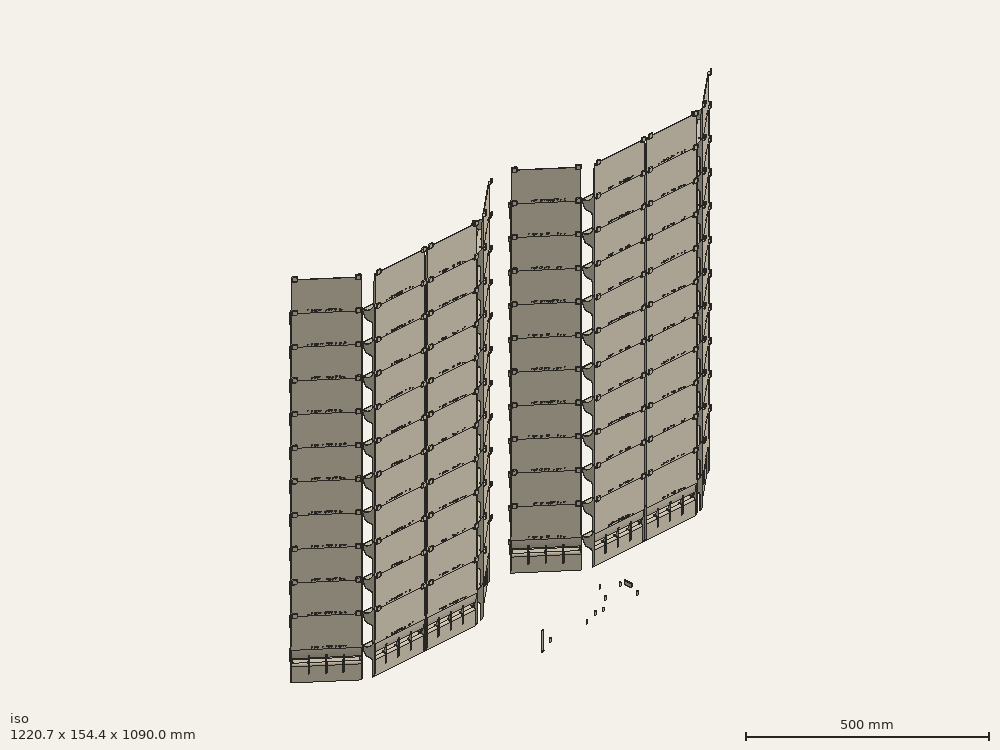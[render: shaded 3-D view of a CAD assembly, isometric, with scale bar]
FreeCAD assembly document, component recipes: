
FREECAD ASSEMBLY — COMPONENT RECIPES ("composit_stand8")

This assembly document has 28 components, labeled P0..P27 below (a component is one placed body or linked part). 26 of them carry a construction recipe — the FreeCAD feature program that regenerates the part from scratch, quoted from this document or its linked companion documents; the rest are supplied as boundary geometry only. No exploded tour is included for this assembly.
NOTE — document 2 of 2 of this assembly tour. The two overview renders and the header above are repeated from document 1; the component sections below continue where the previous document stopped.
COMPONENT P24 — recipe-attached ("module_Body", modeled in this document).
Construction recipe (the document's own serialized feature program — sketch geometry with constraints, then the solid features built on it; lengths are millimeters unless a unit is written):

FEATURE [PartDesign::SubShapeBinder] Binder
  BindCopyOnChange = 0
  BindMode = 0
  ClaimChildren = true
  Context = -> Body [Binder.]
  Fuse = false
  MakeFace = true
  OffsetFill = false
  OffsetIntersection = false
  OffsetJoinType = 0
  OffsetOpenResult = false
  PartialLoad = false
  Relative = false
  Support = -> [Connect]
  _Version = 2
FEATURE [PartDesign::FeaturePython] BaseBend  # WARN: FeaturePython — macro-defined, semantics opaque (R4)
  BendSide = 1
  BendSketch = -> Binder
  MidPlane = false
  Reverse = false
  Suppressed = false
  length = 1100
  radius = 0.1
  thickness = 0.3
  expr: length = <<Properties>>.modules_fix_height
FEATURE [PartDesign::CoordinateSystem] Local_CS005  label="face_base_LCS"
  AttacherType = Attacher::AttachEngine3D
  AttachmentSupport = -> [XY_Plane]
  MapMode = 5
FEATURE [PartDesign::FeaturePython] Extend  # WARN: FeaturePython — macro-defined, semantics opaque (R4)
  BaseFeature = -> BaseBend
  Offset = 0.02
  Refine = true
  Suppressed = false
  UseSubtraction = false
  baseObject = -> BaseBend [Face1]
  gap1 = 0
  gap2 = 0
  length = 0
FEATURE [PartDesign::FeaturePython] Bend  # WARN: FeaturePython — macro-defined, semantics opaque (R4)
  AutoMiter = false
  BaseFeature = -> Extend
  BendType = 0
  LengthList = [0.1]
  LengthSpec = 0
  ReliefFactor = 0.7
  Suppressed = false
  UseReliefFactor = false
  angle = 90
  baseObject = -> Extend [Edge119,Edge104,Edge124,Edge75,Edge58,Edge122,Edge29,Edge14]
  bendAList = [90]
  extend1 = 0
  extend2 = 0
  gap1 = 0
  gap2 = 0
  invert = true
  kfactor = 0.5
  length = 0.1
  maxExtendDist = 5
  minGap = 0.2
  minReliefGap = 1
  miterangle1 = 0
  miterangle2 = 0
  offset = 0
  radius = 0.1
  reliefType = 0
  reliefd = 1
  reliefw = 0.8
  sketchflip = false
  sketchinvert = false
  unfold = false
  expr: radius = BaseBend.radius
FEATURE [PartDesign::CoordinateSystem] Local_CS009  label="face_section_LCS"
  AttacherType = Attacher::AttachEngine3D
  AttachmentOffset = pos=(319.563,20,0) rot=(0,0,1;0rad)
  AttachmentSupport = -> [XY_Plane]
  MapMode = 5
  Placement = pos=(319.563,20,0) rot=(0,0,1;0rad)
  expr: .AttachmentOffset.Base.x = <<mid_Sketch>>.Constraints.middle
  expr: .AttachmentOffset.Base.y = <<base_Sketch>>.Constraints.offset
FEATURE [PartDesign::CoordinateSystem] Local_CS006  label="sink1_LCS"
  AttacherType = Attacher::AttachEngine3D
  AttachmentOffset = pos=(0,0,100) rot=(0,0,1;0rad)
  AttachmentSupport = -> [Local_CS009]
  MapMode = 5
  Placement = pos=(319.563,20,100) rot=(0,0,1;0rad)
  expr: .AttachmentOffset.Base.z = <<sink_placement>>.Placement.Base.z
FEATURE [PartDesign::CoordinateSystem] Local_CS007  label="sink2_LCS"
  AttacherType = Attacher::AttachEngine3D
  AttachmentOffset = pos=(-639.126,0,0) rot=(0,0,1;0rad)
  AttachmentSupport = -> [Local_CS006]
  MapMode = 5
  Placement = pos=(-319.563,20,100) rot=(0,0,1;0rad)
  expr: .AttachmentOffset.Base.x = -<<mid_Sketch>>.Constraints.middle * 2
FEATURE [PartDesign::CoordinateSystem] Local_CS010  label="dropper_comp_fix1_LCS"
  AttacherType = Attacher::AttachEngine3D
  AttachmentOffset = pos=(0,0,1100) rot=(0,0,1;0rad)
  AttachmentSupport = -> [Local_CS009]
  MapMode = 5
  Placement = pos=(319.563,20,1100) rot=(0,0,1;0rad)
  expr: .AttachmentOffset.Base.z = <<Properties>>.modules_fix_height
FEATURE [PartDesign::CoordinateSystem] Local_CS011  label="dropper_comp_fix2_LCS"
  AttacherType = Attacher::AttachEngine3D
  AttachmentOffset = pos=(-639.126,0,0) rot=(0,0,1;0rad)
  AttachmentSupport = -> [Local_CS010]
  MapMode = 5
  Placement = pos=(-319.563,20,1100) rot=(0,0,1;0rad)
  expr: .AttachmentOffset.Base.x = -<<mid_Sketch>>.Constraints.middle * 2
FEATURE [PartDesign::CoordinateSystem] Local_CS014  label="bar1_LCS"
  AttacherType = Attacher::AttachEngine3D
  AttachmentSupport = -> [LinearArray004]
  MapMode = 1
  Placement = pos=(-636.126,17,220) rot=(0.707107,0,0.707107;3.14159rad)
FEATURE [PartDesign::CoordinateSystem] Local_CS015  label="bar2_LCS"
  AttacherType = Attacher::AttachEngine3D
  AttachmentSupport = -> [LinearArray004]
  MapMode = 1
  Placement = pos=(-636.126,17,883.5) rot=(0.707107,0,0.707107;3.14159rad)
FEATURE [PartDesign::CoordinateSystem] Local_CS024
  AttacherType = Attacher::AttachEngine3D
  AttachmentOffset = pos=(319.563,0,0) rot=(0,1,0;3.14159rad)
  AttachmentSupport = -> [XY_Plane]
  MapMode = 5
  Placement = pos=(319.563,0,0) rot=(0,1,0;3.14159rad)
  expr: .AttachmentOffset.Base.x = <<mid_Sketch>>.Constraints.middle
FEATURE [PartDesign::CoordinateSystem] Local_CS025  label="face_lamp_fix_LCS"
  AttacherType = Attacher::AttachEngine3D
  AttachmentOffset = pos=(319.563,0,182) rot=(0,0,1;0rad)
  AttachmentSupport = -> [XY_Plane]
  MapMode = 5
  Placement = pos=(319.563,0,182) rot=(0,0,1;0rad)
  expr: AttachmentOffset = <<face_lamp_fix_placement>>.Placement
FEATURE [PartDesign::CoordinateSystem] Local_CS029
  AttacherType = Attacher::AttachEngine3D
  AttachmentOffset = pos=(164.635,0,0) rot=(0,0,1;0rad)
  AttachmentSupport = -> [Local_CS006]
  MapMode = 5
  Placement = pos=(484.198,20,100) rot=(0,0,1;0rad)
  expr: .AttachmentOffset.Base.x = <<base_Sketch>>.Constraints.face / 2
FEATURE [Sketcher::SketchObject] Sketch075
  AttachmentOffset = pos=(0,0,0) rot=(0,0.707107,0.707107;3.14159rad)
  AttachmentSupport = -> [Local_CS029]
  FullyConstrained = true
  MapMode = 5
  Placement = pos=(484.198,20,100) rot=(0,0.707107,0.707107;3.14159rad)
  expr: Constraints[19] = <<Dimensions>>.Constraints.modules_face / 2
  sketch-geometry (7):
    g0: LineSegment StartX=164.635 StartY=0 StartZ=0 EndX=-1 EndY=0 EndZ=0
    g1: LineSegment StartX=-1 StartY=0 StartZ=0 EndX=-1 EndY=15 EndZ=0
    g2: LineSegment StartX=-1 StartY=15 StartZ=0 EndX=1 EndY=15 EndZ=0
    g3: ArcOfCircle CenterX=1 CenterY=0 CenterZ=0 NormalX=0 NormalY=0 NormalZ=1 AngleXU=0 Radius=15 StartAngle=0.339837 EndAngle=1.5708
    g4: ArcOfCircle CenterX=17.9706 CenterY=6 CenterZ=0 NormalX=0 NormalY=0 NormalZ=1 AngleXU=0 Radius=3 StartAngle=3.48143 EndAngle=4.71239
    g5: LineSegment StartX=164.635 StartY=0 StartZ=0 EndX=164.635 EndY=3 EndZ=0
    g6: LineSegment StartX=164.635 StartY=3 StartZ=0 EndX=17.9706 EndY=3 EndZ=0
  constraints (20):
    c: PointOnObject(g0,g-1)
    c: Horizontal(g0)
    c: Coincident(g0,g1)
    c: Vertical(g1)
    c: Coincident(g1,g2)
    c: Horizontal(g2)
    c: PointOnObject(g3,g-1)
    c: Tangent(g3,g2) = 1.5708
    c: Tangent(g4,g3) = 1.5708
    c: Radius(g4) = 3
    c: Radius(g3) = 15
    c: DistanceX(g2) = 1
    c: DistanceX(g1) = -1
    c: Coincident(g0,g5)
    c: Vertical(g5)
    c: Coincident(g5,g6)
    c: Horizontal(g6)
    c: Tangent(g6,g4) = 1.5708
    c: DistanceY(g5) = 3
    c: DistanceX(g0) = 164.635
FEATURE [Sketcher::SketchObject] Sketch076
  AttachmentOffset = pos=(0,0,0) rot=(0.889126,0.323616,0.323616;1.68804rad)
  AttachmentSupport = -> [Local_CS029]
  FullyConstrained = true
  MapMode = 5
  Placement = pos=(484.198,20,100) rot=(0.889126,0.323616,0.323616;1.68804rad)
  expr: .AttachmentOffset.Rotation.Yaw = <<base_Sketch>>.Constraints.angle
  sketch-geometry (5):
    g0: LineSegment StartX=18.7482 StartY=0 StartZ=0 EndX=-1 EndY=0 EndZ=0
    g1: LineSegment StartX=-1 StartY=0 StartZ=0 EndX=-1 EndY=15 EndZ=0
    g2: LineSegment StartX=-1 StartY=15 StartZ=0 EndX=1 EndY=15 EndZ=0
    g3: ArcOfCircle CenterX=1 CenterY=0 CenterZ=0 NormalX=0 NormalY=0 NormalZ=1 AngleXU=0 Radius=15 StartAngle=0.167448 EndAngle=1.5708
    g4: ArcOfCircle CenterX=18.7482 CenterY=3 CenterZ=0 NormalX=0 NormalY=0 NormalZ=1 AngleXU=0 Radius=3 StartAngle=3.30904 EndAngle=4.71239
  constraints (14):
    c: PointOnObject(g0,g-1)
    c: PointOnObject(g0,g-1)
    c: Coincident(g0,g1)
    c: Vertical(g1)
    c: Coincident(g1,g2)
    c: Horizontal(g2)
    c: PointOnObject(g3,g-1)
    c: Tangent(g3,g2) = 1.5708
    c: Tangent(g4,g0) = 1.5708
    c: Tangent(g4,g3) = 1.5708
    c: DistanceX(g2) = 1
    c: DistanceY(g1,g1) = 15
    c: DistanceX(g1) = -1
    c: Radius(g4) = 3
FEATURE [PartDesign::Plane] DatumPlane004
  AttachmentSupport = -> [Local_CS006]
  Length = 65.8114
  MapMode = 4
  Placement = pos=(319.563,20,100) rot=(0.57735,0.57735,0.57735;2.0944rad)
  ResizeMode = 0
  Width = 140.811
FEATURE [PartDesign::Plane] DatumPlane005
  AttachmentSupport = -> [Local_CS005]
  Length = 60
  MapMode = 4
  Placement = pos=(0,0,0) rot=(0.57735,0.57735,0.57735;2.0944rad)
  ResizeMode = 0
  Width = 60
FEATURE [PartDesign::Mirrored] Mirrored008
  MirrorPlane = -> DatumPlane004
  Suppressed = false
FEATURE [PartDesign::LinearPattern] LinearPattern004
  Direction = -> Sketch075 [H_Axis]
  Length = 639.126
  Mode = 0
  Occurrences = 2
  Offset = 639.126
  Suppressed = false
  expr: Length = <<Dimensions>>.Constraints.modules_middle_distance * 2
FEATURE [PartDesign::CoordinateSystem] Local_CS032  label="face_top_LCS"
  AttacherType = Attacher::AttachEngine3D
  AttachmentOffset = pos=(0,0,1100) rot=(0,0,1;0rad)
  AttachmentSupport = -> [XY_Plane]
  MapMode = 5
  Placement = pos=(0,0,1100) rot=(0,0,1;0rad)
  expr: .AttachmentOffset.Base.z = <<Properties>>.modules_fix_height
FEATURE [PartDesign::CoordinateSystem] Local_CS034
  AttacherType = Attacher::AttachEngine3D
  AttachmentOffset = pos=(-639.126,60,610) rot=(0.57735,-0.57735,-0.57735;2.0944rad)
  AttachmentSupport = -> [XY_Plane]
  MapMode = 5
  Placement = pos=(-639.126,60,610) rot=(0.57735,-0.57735,-0.57735;2.0944rad)
  expr: AttachmentOffset = <<shield_placement>>.Placement
FEATURE [PartDesign::Boolean] Boolean
  BaseFeature = -> Bend
  Group = -> [Compound001]
  Refine = true
  Suppressed = false
  Type = 1
  UsePlacement = false
FEATURE [PartDesign::Boolean] Boolean013
  BaseFeature = -> Boolean
  Group = -> [Compound007]
  Suppressed = false
  Type = 1
  UsePlacement = true
FEATURE [PartDesign::Boolean] Boolean014
  BaseFeature = -> Boolean013
  Group = -> [Compound005]
  Refine = true
  Suppressed = false
  Type = 0
  UsePlacement = true
FEATURE [PartDesign::Pocket] Pocket022
  BaseFeature = -> Boolean014
  Direction = (-1e-16,-1,-2e-16)
  Length = 5
  Length2 = 0.1
  Profile = -> Sketch075
  ReferenceAxis = -> Sketch075 [N_Axis]
  Suppressed = false
  Type = 4
FEATURE [PartDesign::Pocket] Pocket023
  BaseFeature = -> Pocket022
  Direction = (-0.642788,0.766044,-1e-16)
  Length = 0.1
  Length2 = 5
  Midplane = true
  Profile = -> Sketch076
  ReferenceAxis = -> Sketch076 [N_Axis]
  Suppressed = false
  Type = 4
FEATURE [PartDesign::MultiTransform] MultiTransform004
  BaseFeature = -> Pocket023
  Originals = -> [Pocket022,Pocket023]
  Suppressed = false
  Transformations = -> [Mirrored008,LinearPattern004]
FEATURE [PartDesign::Body] Body  label="face"
  Group = -> [Binder,BaseBend,Extend,Bend,Boolean,Boolean013,Local_CS009,Local_CS005,Local_CS006,Local_CS007,Local_CS010,Local_CS011,Local_CS014,Local_CS015,Local_CS024,Local_CS025,Boolean014,Local_CS029,Sketch075,Sketch076,Pocket022,Pocket023,DatumPlane004,DatumPlane005,MultiTransform004,Mirrored008,LinearPattern004,Local_CS032,Local_CS034]
  Origin = -> Origin
  Tip = -> MultiTransform004
COMPONENT P25 — recipe-attached ("composit_electric_shield_fix", modeled in this document).
Construction recipe (the document's own serialized feature program — sketch geometry with constraints, then the solid features built on it; lengths are millimeters unless a unit is written):

FEATURE [PartDesign::SubShapeBinder] Binder003
  BindCopyOnChange = 0
  BindMode = 0
  ClaimChildren = true
  Context = -> Body002 [Binder003.]
  Fuse = false
  MakeFace = true
  OffsetFill = false
  OffsetIntersection = false
  OffsetJoinType = 0
  OffsetOpenResult = false
  PartialLoad = false
  Relative = true
  Support = -> [Connect001]
  _Version = 2
FEATURE [PartDesign::FeaturePython] BaseBend001  # WARN: FeaturePython — macro-defined, semantics opaque (R4)
  BendSide = 0
  BendSketch = -> Binder003
  MidPlane = false
  Reverse = false
  Suppressed = false
  length = 100
  radius = 0.1
  thickness = 0.3
FEATURE [PartDesign::FeaturePython] Extend001  # WARN: FeaturePython — macro-defined, semantics opaque (R4)
  BaseFeature = -> BaseBend001
  Offset = 0.02
  Refine = true
  Suppressed = false
  UseSubtraction = false
  baseObject = -> BaseBend001 [Face1]
  gap1 = 0
  gap2 = 0
  length = 0
FEATURE [PartDesign::FeaturePython] Bend001  # WARN: FeaturePython — macro-defined, semantics opaque (R4)
  AutoMiter = true
  BaseFeature = -> Extend001
  BendType = 1
  LengthList = [15]
  LengthSpec = 0
  ReliefFactor = 0.7
  Suppressed = false
  UseReliefFactor = false
  angle = 90
  baseObject = -> Extend001 [Edge6,Edge8,Edge9,Edge11]
  bendAList = [90]
  extend1 = 0
  extend2 = 0
  gap1 = 0
  gap2 = 0
  invert = true
  kfactor = 0.5
  length = 15
  maxExtendDist = 5
  minGap = 0.2
  minReliefGap = 1
  miterangle1 = 0
  miterangle2 = 0
  offset = 0
  radius = 0.1
  reliefType = 0
  reliefd = 1
  reliefw = 0.8
  sketchflip = false
  sketchinvert = false
  unfold = false
  expr: radius = BaseBend.radius
FEATURE [Sketcher::SketchObject] Sketch031
  AttachmentSupport = -> [XY_Plane003]
  ExternalGeometry = -> [Binder003]
  FullyConstrained = true
  MapMode = 5
  sketch-geometry (13):
    g0: LineSegment StartX=172.194 StartY=8.2 StartZ=0 EndX=172.194 EndY=11.2 EndZ=0
    g1: LineSegment StartX=172.194 StartY=11.2 StartZ=0 EndX=174.122 EndY=8.90187 EndZ=0
    g2: LineSegment StartX=172.194 StartY=8.2 StartZ=0 EndX=173.286 EndY=8.2 EndZ=0
    g3: LineSegment StartX=173.286 StartY=8.2 StartZ=0 EndX=174.122 EndY=8.90187 EndZ=0
    g4: LineSegment StartX=309.163 StartY=122.737 StartZ=0 EndX=309.163 EndY=147 EndZ=0
    g5: LineSegment StartX=309.163 StartY=122.214 StartZ=0 EndX=312.42 EndY=124.947 EndZ=0
    g6: LineSegment StartX=309.163 StartY=122.214 StartZ=0 EndX=308.906 EndY=122.521 EndZ=0
    g7: LineSegment StartX=308.906 StartY=122.521 StartZ=0 EndX=309.163 EndY=122.737 EndZ=0
    g8: LineSegment StartX=312.163 StartY=150 StartZ=0 EndX=312.163 EndY=125.254 EndZ=0
    g9: LineSegment StartX=312.163 StartY=125.254 StartZ=0 EndX=312.42 EndY=124.947 EndZ=0
    g10: LineSegment StartX=309.163 StartY=147 StartZ=0 EndX=311.763 EndY=147 EndZ=0
    g11: LineSegment StartX=311.763 StartY=147 StartZ=0 EndX=311.763 EndY=150 EndZ=0
    g12: LineSegment StartX=311.763 StartY=150 StartZ=0 EndX=312.163 EndY=150 EndZ=0
  constraints (38):
    c: PointOnObject(g0,g-3)
    c: Coincident(g0,g1)
    c: PointOnObject(g1,g-4)
    c: Perpendicular(g-3,g0)
    c: Perpendicular(g-4,g1)
    c: Equal(g1,g0)
    c: DistanceY(g0,g0) = 3
    c: Coincident(g0,g2)
    c: Coincident(g2,g-4)
    c: Coincident(g2,g3)
    c: Coincident(g3,g1)
    c: Vertical(g4)
    c: Coincident(g4,g10)
    c: Coincident(g12,g8)
    c: PointOnObject(g5,g-4)
    c: Vertical(g4,g5)
    c: Coincident(g5,g6)
    c: Coincident(g6,g7)
    c: Distance(g6) = 0.4
    c: Perpendicular(g5,g6)
    c: Perpendicular(g7,g6)
    c: DistanceX(g10,g12) = 3
    c: Coincident(g5,g9)
    c: Coincident(g7,g4)
    c: Coincident(g8,g9)
    c: Vertical(g8)
    c: Perpendicular(g5,g9)
    c: PointOnObject(g-5,g5)
    c: Distance(g9) = 0.4
    c: Coincident(g10,g11)
    c: Horizontal(g10)
    c: Coincident(g11,g12)
    c: Horizontal(g12)
    c: Coincident(g8,g-5)
    c: Vertical(g11)
    c: DistanceY(g11,g11) = 3
    c: DistanceX(g12,g12) = 0.4
    c: Distance(g8,g4) = 3
FEATURE [PartDesign::Pocket] Pocket003
  BaseFeature = -> Bend001
  Direction = (0,0,-1)
  Length = 5
  Length2 = 5
  Midplane = true
  Profile = -> Sketch031
  ReferenceAxis = -> Sketch031 [N_Axis]
  Suppressed = false
  Type = 1
FEATURE [PartDesign::Mirrored] Mirrored
  BaseFeature = -> Pocket003
  MirrorPlane = -> Sketch031 [V_Axis]
  Originals = -> [Pocket003]
  Suppressed = false
FEATURE [PartDesign::CoordinateSystem] Local_CS008
  AttacherType = Attacher::AttachEngine3D
  AttachmentOffset = pos=(0,20,0) rot=(0,0,1;0rad)
  AttachmentSupport = -> [XY_Plane003]
  MapMode = 5
  Placement = pos=(0,20,0) rot=(0,0,1;0rad)
  expr: .AttachmentOffset.Base.y = <<base_Sketch>>.Constraints.offset
FEATURE [PartDesign::CoordinateSystem] Local_CS013  label="dropper_fix_PP_placement"
  AttacherType = Attacher::AttachEngine3D
  AttachmentOffset = pos=(0,0,3) rot=(0,0,1;0rad)
  AttachmentSupport = -> [XY_Plane003]
  MapMode = 5
  Placement = pos=(0,0,3) rot=(0,0,1;0rad)
FEATURE [PartDesign::Boolean] Boolean031
  BaseFeature = -> Mirrored
  Group = -> [Compound039]
  Suppressed = false
  Type = 1
  UsePlacement = true
FEATURE [PartDesign::Boolean] Boolean030
  BaseFeature = -> Boolean031
  Group = -> [Compound038]
  Refine = true
  Suppressed = false
  Type = 0
  UsePlacement = true
FEATURE [PartDesign::Boolean] Boolean002
  BaseFeature = -> Boolean030
  Group = -> [Compound009]
  Suppressed = false
  Type = 1
  UsePlacement = true
FEATURE [PartDesign::Body] Body002  label="dropper_fix_composit"
  Group = -> [Binder003,BaseBend001,Extend001,Sketch031,Bend001,Pocket003,Mirrored,Boolean031,Boolean030,Boolean002,Local_CS008,Local_CS013]
  Origin = -> Origin003
  Tip = -> Boolean002
COMPONENT P26 — geometry summary ("electric_shield_cut"; no construction recipe available for this part):
  bounding box: 315.0 x 88.0 x 10.0 mm
  tessellated surface: 12 triangles
  volume: 277200 mm^3 (100% of its bounding box)
  symmetry: 2-fold rotationally symmetric about the x axis; 2-fold rotationally symmetric about the y axis; 2-fold rotationally symmetric about the z axis; mirror-symmetric across its y mid-plane, z mid-plane
COMPONENT P27 — geometry summary ("modules"; no construction recipe available for this part):
  bounding box: 1220.6 x 970.0 x 137.1 mm
  tessellated surface: 360,096 triangles
  volume: 16054997257454379676075496254509199119899785434639068064063372245540747675981731400751099634202854817792 mm^3 (9887628150821226908688576681887324159217648573793799610549357154315061577400876020368347456602112% of its bounding box)
  symmetry: mirror-symmetric across its x mid-plane
PROVENANCE & LICENSES
A FreeCAD (.FCStd) document from a public repository crawl; recipes are the document's own serialized feature recipes (and, for linked parts, companion documents' recipes).
License: as declared in the source repository (recorded in the dataset sidecar).
